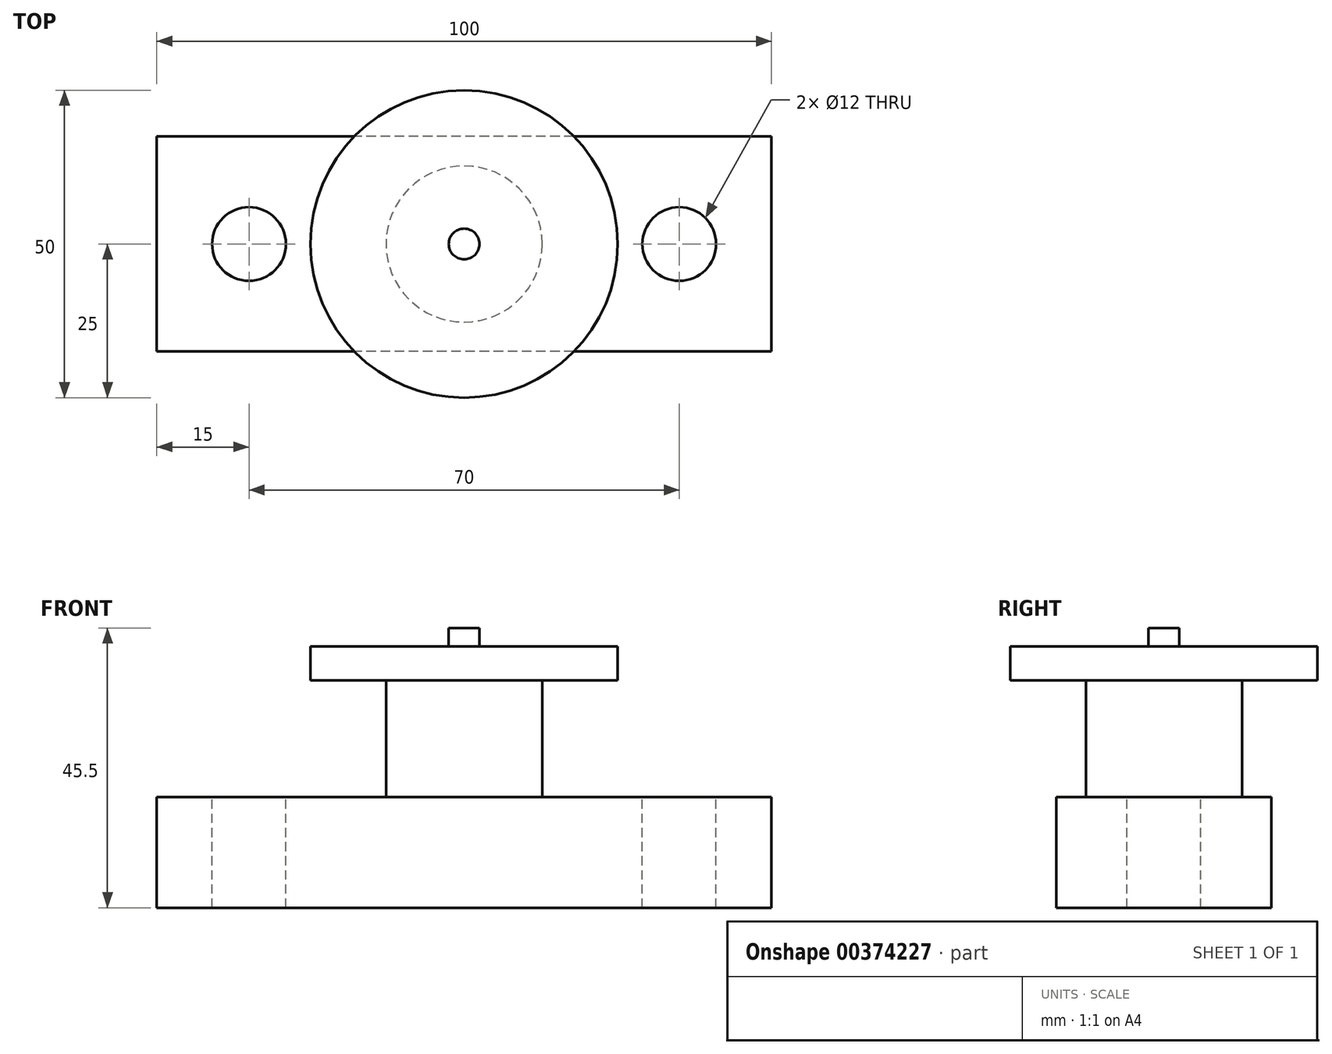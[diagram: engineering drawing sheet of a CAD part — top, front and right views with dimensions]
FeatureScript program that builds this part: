
annotation { "Feature Type Name" : "Feature", "Feature Type Description" : "" }
export const myFeature = defineFeature(function(context is Context, id is Id, definition is map)
    precondition{}
    {
        {
            var Q0;
            Q0=qCreatedBy(makeId("Top.planeOp"),FACE);
            var sketch = newSketch(context, id + "F0", { "sketchPlane" : qUnion([Q0])});
            skLineSegment(sketch, "E0.bottom", {"start": v(50, -17.5) * mm, "end": v(-50, -17.5) * mm});
            skLineSegment(sketch, "E0.top", {"start": v(50, 17.5) * mm, "end": v(-50, 17.5) * mm});
            skLineSegment(sketch, "E0.left", {"start": v(50, -17.5) * mm, "end": v(50, 17.5) * mm});
            skLineSegment(sketch, "E0.right", {"start": v(-50, -17.5) * mm, "end": v(-50, 17.5) * mm});
            skPoint(sketch, "E0.middle", {"position": v(0, 0) * mm});
            skSolve(sketch);
        }
        {
            var Q0;
            Q0=makeQuery(id+"F0.imprint","IMPRINT",FACE,{"disambiguationData":[TD([[makeQuery(id+"F0.imprint","IMPRINT",EDGE,{"derivedFrom":sQuery(id+"F0.wireOp",EDGE,"E0.bottom")}),-1.0]])]});
            extrude(context, id + "F1", {"entities" : qUnion([Q0]), "depth" : -18 * mm});
        }
        {
            var Q0;
            Q0=makeQuery(id+"F1.opExtrude","CAP_FACE",FACE,{"disambiguationData":[OSD([sQuery(id+"F0.wireOp",EDGE,"E0.bottom"),sQuery(id+"F0.wireOp",EDGE,"E0.top"),sQuery(id+"F0.wireOp",EDGE,"E0.left"),sQuery(id+"F0.wireOp",EDGE,"E0.right")])],"isStart":true});
            var sketch = newSketch(context, id + "F2", { "sketchPlane" : qUnion([Q0])});
            skLineSegment(sketch, "E1", {"start": v(50, 0) * mm, "end": v(35, 0) * mm, "construction": true});
            skLineSegment(sketch, "E2", {"start": v(-50, 0) * mm, "end": v(-35, 0) * mm, "construction": true});
            skCircle(sketch, "E3", {"center": v(35, 0) * mm, "radius": 6 * mm});
            skCircle(sketch, "E4", {"center": v(-35, 0) * mm, "radius": 6 * mm});
            skSolve(sketch);
        }
        {
            var Q0;
            Q0=sQuery(id+"F2.wireOp",VERTEX,"E2.end");
            var Q1;
            Q1=sQuery(id+"F2.wireOp",VERTEX,"E3.center");
            var Q2;
            Q2=makeQuery(id+"F1.opExtrude","SWEPT_BODY",BODY,{"disambiguationData":[OSD([sQuery(id+"F0.wireOp",EDGE,"E0.bottom"),sQuery(id+"F0.wireOp",EDGE,"E0.top"),sQuery(id+"F0.wireOp",EDGE,"E0.left"),sQuery(id+"F0.wireOp",EDGE,"E0.right")])]});
            hole(context, id + "F3", {"style" : HoleStyle.SIMPLE, "endStyle" : HoleEndStyle.THROUGH, "holeDiameter" : 12 * mm, "isTappedThrough" : true, "tappedDepth" : 12 * mm, "tapClearance" : 3, "locations" : qUnion([Q0, Q1]), "scope" : qUnion([Q2])});
        }
        {
            var Q0;
            Q0=makeQuery(id+"F1.opExtrude","CAP_FACE",FACE,{"disambiguationData":[OSD([sQuery(id+"F0.wireOp",EDGE,"E0.bottom"),sQuery(id+"F0.wireOp",EDGE,"E0.top"),sQuery(id+"F0.wireOp",EDGE,"E0.left"),sQuery(id+"F0.wireOp",EDGE,"E0.right")])],"isStart":true});
            var sketch = newSketch(context, id + "F4", { "sketchPlane" : qUnion([Q0])});
            skCircle(sketch, "E5", {"center": v(0, 0) * mm, "radius": 12.7 * mm});
            skSolve(sketch);
        }
        {
            var Q0;
            Q0=makeQuery(id+"F4.imprint","IMPRINT",FACE,{"disambiguationData":[TD([[makeQuery(id+"F4.imprint","IMPRINT",EDGE,{"derivedFrom":sQuery(id+"F4.wireOp",EDGE,"E5")}),1.0]])]});
            extrude(context, id + "F5", {"entities" : qUnion([Q0]), "operationType" : NewBodyOperationType.ADD, "depth" : 19 * mm});
        }
        {
            var Q0;
            Q0=makeQuery(id+"F5.opExtrude","CAP_FACE",FACE,{"disambiguationData":[OSD([sQuery(id+"F4.wireOp",EDGE,"E5")])],"isStart":false});
            var sketch = newSketch(context, id + "F6", { "sketchPlane" : qUnion([Q0])});
            skCircle(sketch, "E6", {"center": v(0, 0) * mm, "radius": 25 * mm});
            skSolve(sketch);
        }
        {
            var Q0;
            Q0=makeQuery(id+"F6.imprint","IMPRINT",FACE,{"disambiguationData":[TD([[makeQuery(id+"F6.imprint","IMPRINT",EDGE,{"derivedFrom":sQuery(id+"F6.wireOp",EDGE,"E6")}),1.0]])]});
            var Q1;
            Q1=makeQuery(id+"F6.imprint","IMPRINT",FACE,{"disambiguationData":[TD([[makeQuery(id+"F6.imprint","IMPRINT",EDGE,{"derivedFrom":makeQuery(id+"F5.opExtrude","CAP_EDGE",EDGE,{"disambiguationData":[OSD([sQuery(id+"F4.wireOp",EDGE,"E5")])],"isStart":false})}),1.0]])]});
            extrude(context, id + "F7", {"entities" : qUnion([Q0, Q1]), "operationType" : NewBodyOperationType.ADD, "depth" : 5.5 * mm});
        }
        {
            var Q0;
            Q0=makeQuery(id+"F7.opExtrude","CAP_FACE",FACE,{"disambiguationData":[OSD([sQuery(id+"F6.wireOp",EDGE,"E6")])],"isStart":false});
            var sketch = newSketch(context, id + "F8", { "sketchPlane" : qUnion([Q0])});
            skCircle(sketch, "E7", {"center": v(0, 0) * mm, "radius": 2.5 * mm});
            skSolve(sketch);
        }
        {
            var Q0;
            Q0 = qSketchRegion(id + "F8", true);
            extrude(context, id + "F9", {"entities" : qUnion([Q0]), "operationType" : NewBodyOperationType.ADD, "depth" : 3 * mm});
        }
    });
